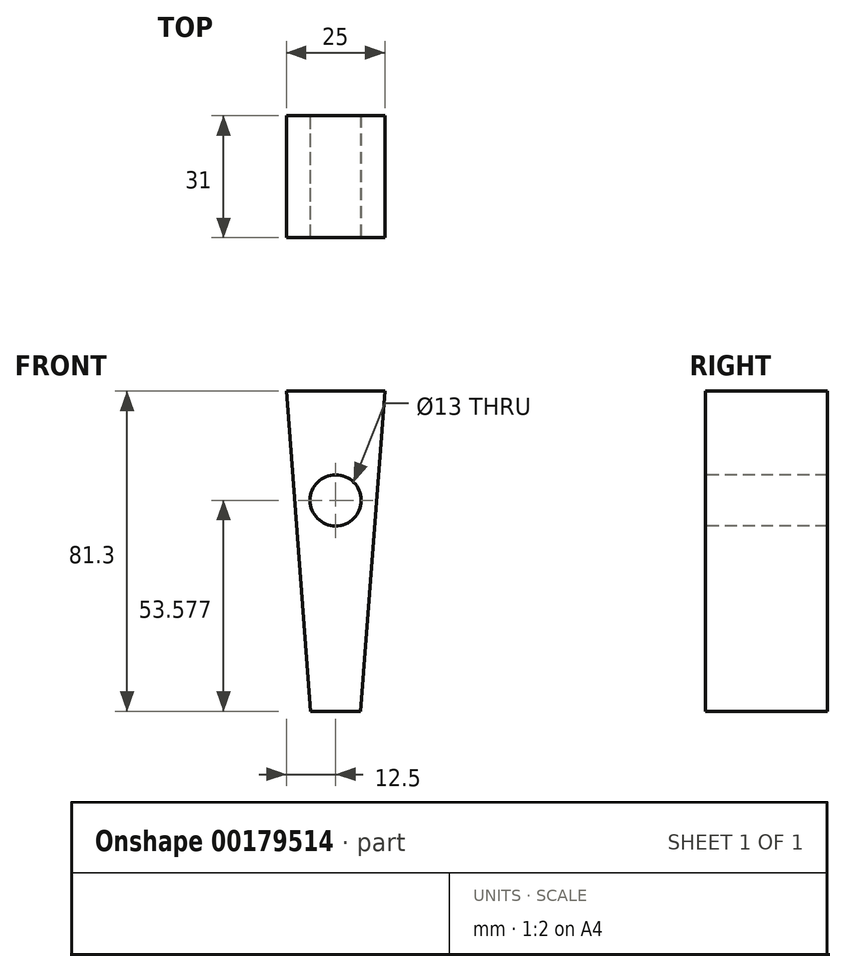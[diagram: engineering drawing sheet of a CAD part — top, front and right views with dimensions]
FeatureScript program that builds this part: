
annotation { "Feature Type Name" : "Feature", "Feature Type Description" : "" }
export const myFeature = defineFeature(function(context is Context, id is Id, definition is map)
    precondition{}
    {
        {
            var Q0;
            Q0=qCreatedBy(makeId("Top.planeOp"),FACE);
            var sketch = newSketch(context, id + "F0", { "sketchPlane" : qUnion([Q0])});
            skLineSegment(sketch, "E0.bottom", {"start": v(-12.5, 15.5) * mm, "end": v(12.5, 15.5) * mm});
            skLineSegment(sketch, "E0.top", {"start": v(-12.5, -15.5) * mm, "end": v(12.5, -15.5) * mm});
            skLineSegment(sketch, "E0.left", {"start": v(-12.5, 15.5) * mm, "end": v(-12.5, -15.5) * mm});
            skLineSegment(sketch, "E0.right", {"start": v(12.5, 15.5) * mm, "end": v(12.5, -15.5) * mm});
            skPoint(sketch, "E0.middle", {"position": v(0, 0) * mm});
            skSolve(sketch);
        }
        {
            var Q0;
            Q0=qSketchRegion(id+"F0",true);
            extrude(context, id + "F1", {"entities" : qUnion([Q0]), "depth" : 86.3 * mm});
        }
        {
            var Q0;
            Q0=qCreatedBy(makeId("Front.planeOp"),FACE);
            var sketch = newSketch(context, id + "F2", { "sketchPlane" : qUnion([Q0])});
            skCircle(sketch, "E1", {"center": v(0, 58.58) * mm, "radius": 6.5 * mm});
            skSolve(sketch);
        }
        {
            var Q0;
            Q0=qSketchRegion(id+"F2",true);
            extrude(context, id + "F3", {"entities" : qUnion([Q0]), "operationType" : NewBodyOperationType.REMOVE, "endBound" : BoundingType.SYMMETRIC, "oppositeDirection" : true, "depth" : 63 * mm});
        }
        {
            var Q0;
            Q0=makeQuery(id+"F1.opExtrude","SWEPT_FACE",FACE,{"disambiguationData":[OSD([sQuery(id+"F0.wireOp",EDGE,"E0.bottom")])]});
            var sketch = newSketch(context, id + "F4", { "sketchPlane" : qUnion([Q0])});
            skLineSegment(sketch, "E2", {"start": v(-12.5, 86.3) * mm, "end": v(-6, 0) * mm});
            skLineSegment(sketch, "E3", {"start": v(-6, 0) * mm, "end": v(6, 0) * mm});
            skLineSegment(sketch, "E4", {"start": v(6, 0) * mm, "end": v(12.5, 86.3) * mm});
            skSolve(sketch);
        }
        {
            var Q0;
            {var subQ0=sQuery(id+"F4.wireOp",EDGE,"E4");Q0=makeQuery(id+"F4.imprint","IMPRINT",FACE,{"disambiguationData":[TD([[makeQuery(id+"F4.imprint","IMPRINT",EDGE,{"derivedFrom":subQ0}),-1.0]])]});}
            var Q1;
            {var subQ0=sQuery(id+"F4.wireOp",EDGE,"E2");Q1=makeQuery(id+"F4.imprint","IMPRINT",FACE,{"disambiguationData":[TD([[makeQuery(id+"F4.imprint","IMPRINT",EDGE,{"derivedFrom":subQ0}),-1.0]])]});}
            extrude(context, id + "F5", {"entities" : qUnion([Q0, Q1]), "operationType" : NewBodyOperationType.REMOVE, "endBound" : BoundingType.THROUGH_ALL, "oppositeDirection" : true, "depth" : 25 * mm});
        }
        {
            var Q0;
            Q0=qCreatedBy(makeId("Front.planeOp"),FACE);
            var sketch = newSketch(context, id + "F6", { "sketchPlane" : qUnion([Q0])});
            skLineSegment(sketch, "E5.bottom", {"start": v(-10, 0) * mm, "end": v(10, 0) * mm});
            skLineSegment(sketch, "E5.top", {"start": v(-10, 5) * mm, "end": v(10, 5) * mm});
            skLineSegment(sketch, "E5.left", {"start": v(-10, 0) * mm, "end": v(-10, 5) * mm});
            skLineSegment(sketch, "E5.right", {"start": v(10, 0) * mm, "end": v(10, 5) * mm});
            skSolve(sketch);
        }
        {
            var Q0;
            Q0=makeQuery(id+"F6.imprint","IMPRINT",FACE,{"disambiguationData":[TD([[makeQuery(id+"F6.imprint","IMPRINT",EDGE,{"derivedFrom":sQuery(id+"F6.wireOp",EDGE,"E5.bottom")}),1.0]])]});
            extrude(context, id + "F7", {"entities" : qUnion([Q0]), "operationType" : NewBodyOperationType.REMOVE, "endBound" : BoundingType.SYMMETRIC, "depth" : 100 * mm});
        }
    });
